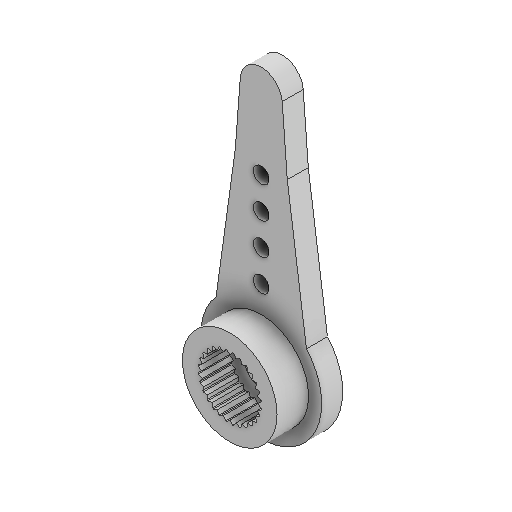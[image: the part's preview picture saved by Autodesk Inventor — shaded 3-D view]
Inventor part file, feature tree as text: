
AUTODESK INVENTOR PART (.ipt)
format: ipt  version: 2025.1 (Build 291241000, 241)  size: 242,176 bytes
history: native  units: mm
features: other x2, extrude x2, sketch x2, fillet x1
ambient origin geometry x8: Origin, YZ Plane, XZ Plane, XY Plane, X Axis, Y Axis, Z Axis, Center Point
bodies: Body1 (feature_tree)
feature tree (7):
  other  "Bryła1"
  extrude  "Wyciągnięcie proste1"  Depth=10.0mm TaperAngle=0.0deg
  extrude  "Wyciągnięcie proste2"  Depth=10.0mm TaperAngle=0.0deg
  fillet  "Zaokrąglenie1"  Radius=2.0mm
  sketch  "Szkic1"
  sketch  "Szkic4"
  other  "Enlèv. mat.-Extru.5"
